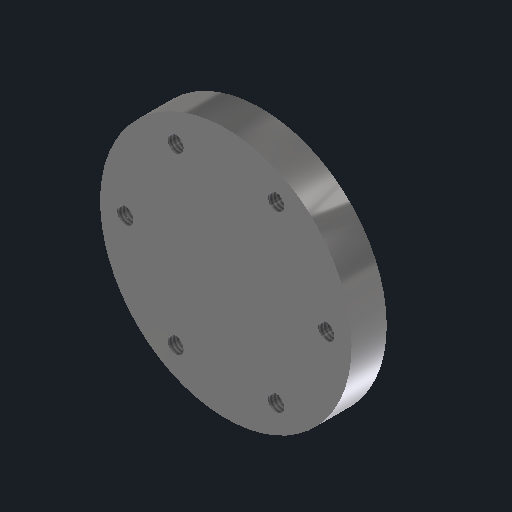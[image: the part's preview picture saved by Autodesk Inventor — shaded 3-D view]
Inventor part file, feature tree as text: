
AUTODESK INVENTOR PART (.ipt)
format: ipt  version: 2022 (Build 260153000, 153)  size: 157,696 bytes
history: native  units: mm
features: sketch x4, projected_geometry x3, extrude x2, hole x2, reference x2, other x2, chamfer x1, plane x1
ambient origin geometry x8: Origin, YZ Plane, XZ Plane, XY Plane, X Axis, Y Axis, Z Axis, Center Point
bodies: Solid1 (feature_tree)
feature tree (17):
  extrude  "Extrusion1"  Depth=10.0mm
  extrude  "Extrusion2"  Depth=2.0mm TaperAngle=0.0deg
  chamfer  "Chamfer1"  Distance=3.0mm Angle=30.0deg
  plane  "Work Plane1"
  hole  "Hole2"  [1 undecoded]
  hole  "Hole3"  [1 undecoded]
  sketch  "Sketch1"  dims[d0=10.0mm d1=0.0mm d2=4.0mm]
  reference  "Reference1"
  sketch  "Sketch2"  dims[d3=50.0mm d4=2.0mm d5=0.0mm d6=3.0mm d7=2.0mm d8=30.0deg]
  projected_geometry  "Projected Loop1"
  sketch  "Sketch4"  dims[d20=2.459mm d21=6.0mm d22=13.0mm d23=3.4mm d24=90.0deg d25=8.8mm d26=20.594885mm d27=5.0mm d28=0.0mm]
  reference  "Reference2"
  projected_geometry  "Projected Loop2"
  sketch  "Sketch5"  dims[d29=4.0mm d30=40.0mm d31=60.0mm d33=360.0deg d35=3.242mm d36=5.0mm d37=4.0mm d38=2.0mm d39=90.0deg d40=6.0mm d41=20.594885mm d32=0.872665mm]
  projected_geometry  "Projected Loop3"
  other  "SistemaDeElevación.iam"
  other  "Tornillo de elevación:1"
note: 2 required parameter values undecoded (feature->parameter linkage not recoverable at this tier; creation-order binding heuristic only, values carry confidence <= 0.55)
